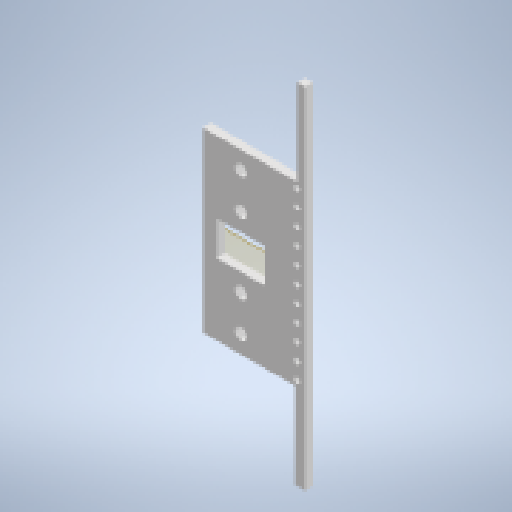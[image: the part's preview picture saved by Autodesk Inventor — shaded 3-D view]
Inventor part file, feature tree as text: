
AUTODESK INVENTOR PART (.ipt)
format: ipt  version: 2024.2 (Build 282272000, 272)  size: 202,752 bytes
history: native  units: mm
features: other x6, extrude x1, sketch x1
ambient origin geometry x8: Origin, YZ Plane, XZ Plane, XY Plane, X Axis, Y Axis, Z Axis, Center Point
bodies: Solide1 (feature_tree)
feature tree (8):
  other  "Plan de construction1"
  extrude  "Extrusion1"  Depth=38.5mm
  sketch  "Esquisse1"
  other  "Référence1"
  other  "<userpath>\Desktop\meca_robotbebou\embasev2\embasev2.iam"
  other  "embasev2.iam"
  other  "moyeu_MIR1:1"
  other  "support_moteur_v3:1"
